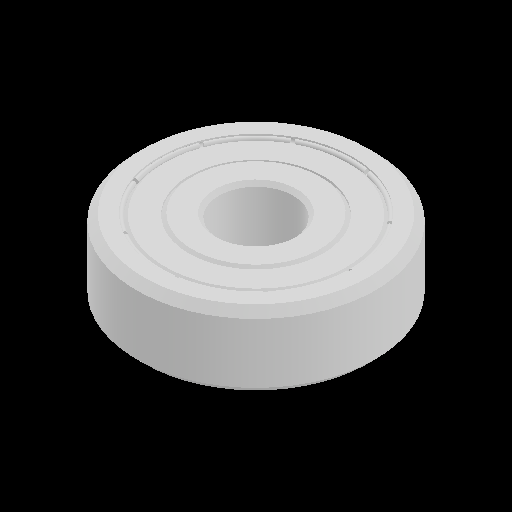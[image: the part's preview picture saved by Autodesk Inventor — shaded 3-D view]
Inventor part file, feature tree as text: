
AUTODESK INVENTOR PART (.ipt)
format: ipt  version: 2023 (Build 270158000, 158)  size: 300,544 bytes
history: native  units: mm
features: mirror x9, other x8, revolve x2
ambient origin geometry x8: Origin, YZ Plane, XZ Plane, XY Plane, X Axis, Y Axis, Z Axis, Center Point
bodies: Solid1 (feature_tree), Solid2 (feature_tree), Solid3 (feature_tree), Solid4 (feature_tree), Solid5 (feature_tree), Solid6 (feature_tree), Solid7 (feature_tree), Solid8 (feature_tree), Solid9 (feature_tree), Solid10 (feature_tree), Solid11 (feature_tree), Solid12 (feature_tree), Solid13 (feature_tree), Solid14 (feature_tree), Solid15 (feature_tree), Solid16 (feature_tree), Solid17 (feature_tree), Solid18 (feature_tree), Solid19 (feature_tree)
feature tree (19):
  revolve  "Revolve1"  [1 undecoded]
  revolve  "Revolve2"  [1 undecoded]
  other  "CirPattern1[1]"
  other  "CirPattern1[2]"
  other  "CirPattern1[3]"
  other  "CirPattern1[4]"
  other  "CirPattern1[5]"
  other  "CirPattern1[6]"
  other  "CirPattern1[7]"
  other  "CirPattern1[8]"
  mirror  "Mirror1[1]"
  mirror  "Mirror1[2]"
  mirror  "Mirror1[3]"
  mirror  "Mirror1[4]"
  mirror  "Mirror1[5]"
  mirror  "Mirror1[6]"
  mirror  "Mirror1[7]"
  mirror  "Mirror1[8]"
  mirror  "Mirror1[9]"
note: 2 required parameter values undecoded (feature->parameter linkage not recoverable at this tier; creation-order binding heuristic only, values carry confidence <= 0.55)
